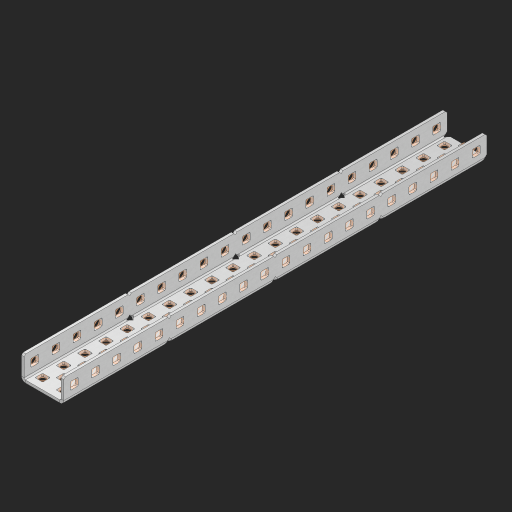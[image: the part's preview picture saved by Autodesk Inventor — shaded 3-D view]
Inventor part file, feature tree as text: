
AUTODESK INVENTOR PART (.ipt)
format: ipt  version: 2023 (Build 270158000, 158)  size: 1,400,320 bytes
history: native  units: in
note: dims shown in document units (in); Inventor stores cm internally (conversion verified against a paired STEP export)
features: other x107, extrude x98, sheet_metal_op x11, sketch x10, pattern_linear x2, mirror x1, chamfer x1
ambient origin geometry x8: Origin, YZ Plane, XZ Plane, XY Plane, X Axis, Y Axis, Z Axis, Center Point
bodies: Solid1 (feature_tree), Body (feature_tree)
feature tree (230):
  sheet_metal_op  "Flanges"
  other  "Flange Pattern Plane"
  other  "Flange Pattern Sketch"
  sheet_metal_op  "Flange Pattern"
  sheet_metal_op  "Body Pattern"
  pattern_linear  "Center Pattern"  Spacing1=0.0625in  [1 undecoded]
  other  "Arc Length"
  mirror  "Notch Mirror"
  pattern_linear  "Notch Pattern"  Spacing1=0.182in  [1 undecoded]
  chamfer  "End Chamfer"
  extrude  "Half Cut"  Depth=0.02in
  sketch  "Sketch1"  dims[d0=1.0in]
  other  "Plate1"
  sketch  "Sketch2"  dims[d1=10.0in]
  other  "Plate2"
  sheet_metal_op  "Bend1"
  sheet_metal_op  "Corner1"
  sketch  "Sketch3"  dims[d2=0.0625in]
  sketch  "Sketch7"  dims[d3=0.0625in]
  other  "Srf1"
  other  "Srf2"
  sketch  "Sketch8"  dims[d4=0.0312in]
  sketch  "Sketch9"  dims[d5=0.125in]
  other  "Srf91"
  sheet_metal_op  "Body Pattern Sketch"
  other  "Srf92"
  sketch  "Sketch13"  dims[d6=0.0625in]
  sketch  "Sketch14"  dims[d7=0.5in d8=90.0deg d9=0.0312in]
  sketch  "Sketch15"  dims[d10=0.25in]
  sketch  "Sketch16"  dims[d11=0.0625in d12=0.0625in d16=0.182in d17=0.02in d18=0.0625in d19=0.0in d20=0.25in d21=0.25in d38=7.874in d40=0.5in d41=0.7874in d43=1.0in d46=0.172in d47=1.0in d48=0.0in d49=0.182in d50=0.02in d51=0.25in d52=0.25in d53=0.0625in d54=0.0in d55=0.172in d56=1.0in d57=0.0in d58=0.25in d60=7.874in d62=0.5in d63=0.7874in d65=0.5in d85=0.1473in d86=0.1782in d88=0.04in d89=0.0625in d90=0.0in d91=0.04in d92=0.0491in d95=2.5in d96=0.04in d97=0.25in d98=45.0deg d99=0.25in d100=0.5in d101=0.0in d102=2.497in d106=0.182in d107=0.02in d108=0.5in d109=0.5in d110=0.0625in d111=0.0in d112=0.172in d113=0.5in d114=0.0in d117=0.5in d118=0.5in d119=0.5in]
  other  "Srf786"
  other  "Srf823"
  other  "Srf824"
  other  "Srf825"
  other  "Srf826"
  other  "Srf827"
  other  "Srf828"
  other  "Srf829"
  other  "Srf856"
  other  "Srf857"
  other  "Srf858"
  other  "Srf859"
  other  "Srf860"
  other  "Srf861"
  other  "Srf862"
  other  "Srf889"
  other  "Srf890"
  other  "Srf891"
  other  "Srf892"
  other  "Srf893"
  other  "Srf894"
  other  "Srf895"
  other  "Srf896"
  other  "Srf922"
  other  "Srf923"
  other  "Srf924"
  other  "Srf925"
  other  "Srf926"
  other  "Srf959"
  other  "Srf960"
  other  "Srf961"
  other  "Srf962"
  other  "Srf963"
  other  "Srf996"
  other  "Srf997"
  other  "Srf998"
  other  "Srf999"
  other  "Srf1000"
  other  "Srf1143"
  other  "Srf1144"
  other  "Srf1145"
  other  "Srf1146"
  other  "Srf1147"
  other  "Srf1148"
  other  "Srf1149"
  other  "Srf1150"
  other  "Srf1151"
  other  "Srf1152"
  other  "Srf1153"
  other  "Srf1154"
  other  "Srf1155"
  other  "Srf1156"
  other  "Srf1157"
  other  "Srf1158"
  other  "Srf1159"
  other  "Srf1160"
  other  "Srf1161"
  other  "Srf1162"
  other  "Srf1163"
  other  "Srf1164"
  other  "Srf1165"
  other  "Srf1166"
  other  "Srf1167"
  other  "Srf1168"
  other  "Srf1199"
  other  "Srf1200"
  other  "Srf1201"
  other  "Srf1202"
  other  "Srf1203"
  other  "Srf1204"
  other  "Srf1205"
  other  "Srf1206"
  other  "Srf1207"
  other  "Srf1208"
  other  "Srf1209"
  other  "Srf1210"
  other  "Srf1211"
  other  "Srf1212"
  other  "Srf1213"
  other  "Srf1214"
  other  "Srf1215"
  other  "Srf1216"
  other  "Srf1217"
  other  "Srf1218"
  other  "Srf1219"
  other  "Srf1220"
  other  "Srf1221"
  other  "Srf1222"
  other  "Srf1223"
  other  "Srf1224"
  other  "Srf1255"
  other  "Srf1256"
  other  "Srf1257"
  other  "Srf1258"
  other  "Srf1259"
  other  "Srf1260"
  sheet_metal_op  "Flange Stamp"
  sheet_metal_op  "Flange Circle"
  sheet_metal_op  "Body Stamp"
  sheet_metal_op  "Body Circle"
  other  "Center Stamp"
  other  "Center Circle"
  sheet_metal_op  "Notch"
  extrude  "ExtrusionSrf2"  Depth=0.0625in
  extrude  "ExtrusionSrf92"  TaperAngle=0.0deg  [1 undecoded]
  extrude  "ExtrusionSrf823"  Depth=0.5in
  extrude  "ExtrusionSrf824"  Depth=0.5in
  extrude  "ExtrusionSrf825"  Depth=0.5in
  extrude  "ExtrusionSrf826"  Depth=0.5in
  extrude  "ExtrusionSrf827"  Depth=1.0in TaperAngle=0.0deg
  extrude  "ExtrusionSrf828"  Depth=0.5in
  extrude  "ExtrusionSrf829"  Depth=0.02in
  extrude  "ExtrusionSrf856"  Depth=0.5in
  extrude  "ExtrusionSrf857"  Depth=0.5in
  extrude  "ExtrusionSrf858"  Depth=0.0625in
  extrude  "ExtrusionSrf859"  TaperAngle=0.0deg  [1 undecoded]
  extrude  "ExtrusionSrf860"  Depth=0.5in
  extrude  "ExtrusionSrf861"  Depth=1.0in TaperAngle=0.0deg
  extrude  "ExtrusionSrf862"  Depth=0.5in
  extrude  "ExtrusionSrf889"  Depth=0.5in
  extrude  "ExtrusionSrf890"  Depth=0.5in
  extrude  "ExtrusionSrf891"  Depth=0.5in
  extrude  "ExtrusionSrf892"  Depth=0.5in
  extrude  "ExtrusionSrf893"  Depth=0.5in
  extrude  "ExtrusionSrf894"  Depth=0.0625in
  extrude  "ExtrusionSrf895"  TaperAngle=0.0deg  [1 undecoded]
  extrude  "ExtrusionSrf896"  Depth=0.5in
  extrude  "ExtrusionSrf922"  Depth=0.5in
  extrude  "ExtrusionSrf923"  Depth=2.5in
  extrude  "ExtrusionSrf924"  Depth=0.5in TaperAngle=45.0deg
  extrude  "ExtrusionSrf925"  Depth=0.5in
  extrude  "ExtrusionSrf926"  Depth=0.5in TaperAngle=0.0deg
  extrude  "ExtrusionSrf959"  Depth=0.5in
  extrude  "ExtrusionSrf960"  Depth=0.5in
  extrude  "ExtrusionSrf961"  Depth=0.02in
  extrude  "ExtrusionSrf962"  Depth=0.5in
  extrude  "ExtrusionSrf963"  Depth=0.5in
  extrude  "ExtrusionSrf996"  Depth=0.0625in
  extrude  "ExtrusionSrf997"  TaperAngle=0.0deg  [1 undecoded]
  extrude  "ExtrusionSrf998"  Depth=0.5in
  extrude  "ExtrusionSrf999"  Depth=0.5in TaperAngle=0.0deg
  extrude  "ExtrusionSrf1000"  Depth=0.5in
  extrude  "ExtrusionSrf1143"  Depth=0.5in
  extrude  "ExtrusionSrf1144"  Depth=0.5in
  extrude  "ExtrusionSrf1145"  [1 undecoded]
  extrude  "ExtrusionSrf1146"  [1 undecoded]
  extrude  "ExtrusionSrf1147"  [1 undecoded]
  extrude  "ExtrusionSrf1148"  [1 undecoded]
  extrude  "ExtrusionSrf1149"  [1 undecoded]
  extrude  "ExtrusionSrf1150"  [1 undecoded]
  extrude  "ExtrusionSrf1151"  [1 undecoded]
  extrude  "ExtrusionSrf1152"  [1 undecoded]
  extrude  "ExtrusionSrf1153"  [1 undecoded]
  extrude  "ExtrusionSrf1154"  [1 undecoded]
  extrude  "ExtrusionSrf1155"  [1 undecoded]
  extrude  "ExtrusionSrf1156"  [1 undecoded]
  extrude  "ExtrusionSrf1157"  [1 undecoded]
  extrude  "ExtrusionSrf1158"  [1 undecoded]
  extrude  "ExtrusionSrf1159"  [1 undecoded]
  extrude  "ExtrusionSrf1160"  [1 undecoded]
  extrude  "ExtrusionSrf1161"  [1 undecoded]
  extrude  "ExtrusionSrf1162"  [1 undecoded]
  extrude  "ExtrusionSrf1163"  [1 undecoded]
  extrude  "ExtrusionSrf1164"  [1 undecoded]
  extrude  "ExtrusionSrf1165"  [1 undecoded]
  extrude  "ExtrusionSrf1166"  [1 undecoded]
  extrude  "ExtrusionSrf1167"  [1 undecoded]
  extrude  "ExtrusionSrf1168"  [1 undecoded]
  extrude  "ExtrusionSrf1199"  [1 undecoded]
  extrude  "ExtrusionSrf1200"  [1 undecoded]
  extrude  "ExtrusionSrf1201"  [1 undecoded]
  extrude  "ExtrusionSrf1202"  [1 undecoded]
  extrude  "ExtrusionSrf1203"  [1 undecoded]
  extrude  "ExtrusionSrf1204"  [1 undecoded]
  extrude  "ExtrusionSrf1205"  [1 undecoded]
  extrude  "ExtrusionSrf1206"  [1 undecoded]
  extrude  "ExtrusionSrf1207"  [1 undecoded]
  extrude  "ExtrusionSrf1208"  [1 undecoded]
  extrude  "ExtrusionSrf1209"  [1 undecoded]
  extrude  "ExtrusionSrf1210"  [1 undecoded]
  extrude  "ExtrusionSrf1211"  [1 undecoded]
  extrude  "ExtrusionSrf1212"  [1 undecoded]
  extrude  "ExtrusionSrf1213"  [1 undecoded]
  extrude  "ExtrusionSrf1214"  [1 undecoded]
  extrude  "ExtrusionSrf1215"  [1 undecoded]
  extrude  "ExtrusionSrf1216"  [1 undecoded]
  extrude  "ExtrusionSrf1217"  [1 undecoded]
  extrude  "ExtrusionSrf1218"  [1 undecoded]
  extrude  "ExtrusionSrf1219"  [1 undecoded]
  extrude  "ExtrusionSrf1220"  [1 undecoded]
  extrude  "ExtrusionSrf1221"  [1 undecoded]
  extrude  "ExtrusionSrf1222"  [1 undecoded]
  extrude  "ExtrusionSrf1223"  [1 undecoded]
  extrude  "ExtrusionSrf1224"  [1 undecoded]
  extrude  "ExtrusionSrf1255"  [1 undecoded]
  extrude  "ExtrusionSrf1256"  [1 undecoded]
  extrude  "ExtrusionSrf1257"  [1 undecoded]
  extrude  "ExtrusionSrf1258"  [1 undecoded]
  extrude  "ExtrusionSrf1259"  [1 undecoded]
  extrude  "ExtrusionSrf1260"  [1 undecoded]
note: 62 required parameter values undecoded (feature->parameter linkage not recoverable at this tier; creation-order binding heuristic only, values carry confidence <= 0.55)
